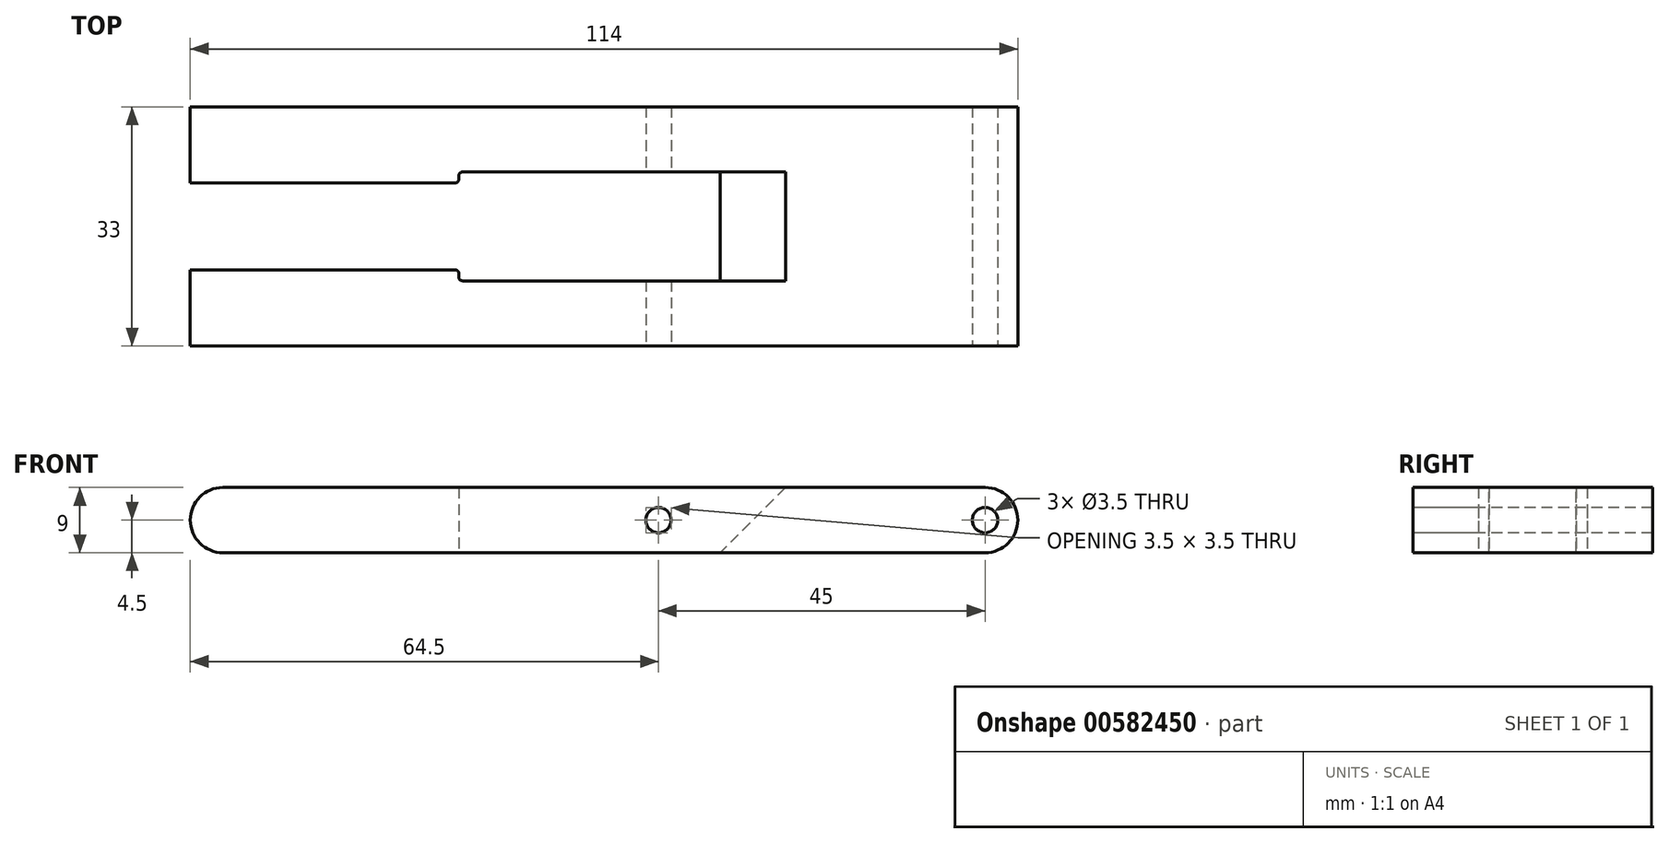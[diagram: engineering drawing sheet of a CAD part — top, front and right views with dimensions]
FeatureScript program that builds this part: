
annotation { "Feature Type Name" : "Feature", "Feature Type Description" : "" }
export const myFeature = defineFeature(function(context is Context, id is Id, definition is map)
    precondition{}
    {
        {
            var Q0;
            Q0=qCreatedBy(makeId("Front.planeOp"),FACE);
            var sketch = newSketch(context, id + "F0", { "sketchPlane" : qUnion([Q0])});
            skLineSegment(sketch, "E0", {"start": v(-52.5, 0) * mm, "end": v(52.5, 0) * mm});
            skLineSegment(sketch, "E1", {"start": v(-52.5, 9) * mm, "end": v(52.5, 9) * mm});
            skArc(sketch, "E2", {"start": v(52.5, 0) * mm, "mid": v(57, 4.5) * mm, "end": v(52.5, 9) * mm});
            skArc(sketch, "E3", {"start": v(-52.5, 9) * mm, "mid": v(-57, 4.5) * mm, "end": v(-52.5, 0) * mm});
            skSolve(sketch);
        }
        {
            var Q0;
            Q0 = qSketchRegion(id + "F0", true);
            extrude(context, id + "F1", {"entities" : qUnion([Q0]), "endBound" : BoundingType.SYMMETRIC, "depth" : 33 * mm, "offsetDistance" : 25 * mm});
        }
        {
            var Q0;
            Q0=makeQuery(id+"F1.opExtrude","CAP_FACE",FACE,{"disambiguationData":[OSD([sQuery(id+"F0.wireOp",EDGE,"aJSWKm7K-i3MK-chJk-4c2A-e9u8y67YIx2B"),sQuery(id+"F0.wireOp",EDGE,"E0"),sQuery(id+"F0.wireOp",EDGE,"E1"),sQuery(id+"F0.wireOp",EDGE,"E2")])],"isStart":false});
            var sketch = newSketch(context, id + "F2", { "sketchPlane" : qUnion([Q0])});
            skLineSegment(sketch, "E4.bottom", {"start": v(52.5, 4.5) * mm, "end": v(7.5, 4.5) * mm});
            skLineSegment(sketch, "E4.top", {"start": v(52.5, 14.5) * mm, "end": v(7.5, 14.5) * mm});
            skLineSegment(sketch, "E4.left", {"start": v(52.5, 4.5) * mm, "end": v(52.5, 14.5) * mm});
            skLineSegment(sketch, "E4.right", {"start": v(7.5, 4.5) * mm, "end": v(7.5, 14.5) * mm});
            skSolve(sketch);
        }
        {
            var Q0;
            Q0=sQuery(id+"F2.wireOp",VERTEX,"E4.right.start");
            var Q1;
            Q1=sQuery(id+"F2.wireOp",VERTEX,"E4.left.start");
            var Q2;
            Q2=makeQuery(id+"F1.opExtrude","SWEPT_BODY",BODY,{"disambiguationData":[OSD([sQuery(id+"F0.wireOp",EDGE,"aJSWKm7K-i3MK-chJk-4c2A-e9u8y67YIx2B"),sQuery(id+"F0.wireOp",EDGE,"E0"),sQuery(id+"F0.wireOp",EDGE,"E1"),sQuery(id+"F0.wireOp",EDGE,"E2")])]});
            hole(context, id + "F3", {"style" : HoleStyle.SIMPLE, "endStyle" : HoleEndStyle.THROUGH, "holeDiameter" : 3.5 * mm, "majorDiameter" : 5 * mm, "tappedDepth" : 12 * mm, "tapClearance" : 3, "locations" : qUnion([Q0, Q1]), "scope" : qUnion([Q2])});
        }
        {
            var Q0;
            Q0=qCreatedBy(makeId("Top.planeOp"),FACE);
            var sketch = newSketch(context, id + "F4", { "sketchPlane" : qUnion([Q0])});
            skLineSegment(sketch, "E5.bottom", {"start": v(-20, 7.5) * mm, "end": v(15, 7.5) * mm});
            skLineSegment(sketch, "E5.top", {"start": v(-20, -7.5) * mm, "end": v(15, -7.5) * mm});
            skLineSegment(sketch, "E5.left", {"start": v(-20, 7.5) * mm, "end": v(-20, -7.5) * mm});
            skLineSegment(sketch, "E5.right", {"start": v(15, 7.5) * mm, "end": v(15, -7.5) * mm});
            skLineSegment(sketch, "E6.bottom", {"start": v(-60, 6) * mm, "end": v(-20, 6) * mm});
            skLineSegment(sketch, "E6.top", {"start": v(-60, -6) * mm, "end": v(-20, -6) * mm});
            skLineSegment(sketch, "E6.left", {"start": v(-60, 6) * mm, "end": v(-60, -6) * mm});
            skLineSegment(sketch, "E6.right", {"start": v(-20, 6) * mm, "end": v(-20, -6) * mm});
            skSolve(sketch);
        }
        {
            var Q0;
            Q0 = qSketchRegion(id + "F4", true);
            extrude(context, id + "F5", {"entities" : qUnion([Q0]), "depth" : 25 * mm, "offsetDistance" : 25 * mm});
        }
        {
            var Q0;
            Q0=makeQuery(id+"F5.opExtrude","SWEPT_BODY",BODY,{"disambiguationData":[OSD([sQuery(id+"F63sIpcFp3KkyEQ_1.wireOp",EDGE,"vlWsCU3u-YBZQ-iikB-UPRL-M2tObz70Hnuf.bottom"),sQuery(id+"F63sIpcFp3KkyEQ_1.wireOp",EDGE,"vlWsCU3u-YBZQ-iikB-UPRL-M2tObz70Hnuf.top"),sQuery(id+"F63sIpcFp3KkyEQ_1.wireOp",EDGE,"vlWsCU3u-YBZQ-iikB-UPRL-M2tObz70Hnuf.left"),sQuery(id+"F63sIpcFp3KkyEQ_1.wireOp",EDGE,"vlWsCU3u-YBZQ-iikB-UPRL-M2tObz70Hnuf.right")])]});
            var Q1;
            Q1=makeQuery(id+"F5.opExtrude","SWEPT_BODY",BODY,{"disambiguationData":[OSD([sQuery(id+"F4.wireOp",EDGE,"E5.bottom"),sQuery(id+"F4.wireOp",EDGE,"E5.top"),sQuery(id+"F4.wireOp",EDGE,"E5.left"),sQuery(id+"F4.wireOp",EDGE,"E5.right")])]});
            var Q2;
            Q2=makeQuery(id+"F1.opExtrude","SWEPT_BODY",BODY,{"disambiguationData":[OSD([sQuery(id+"F0.wireOp",EDGE,"aJSWKm7K-i3MK-chJk-4c2A-e9u8y67YIx2B"),sQuery(id+"F0.wireOp",EDGE,"E0"),sQuery(id+"F0.wireOp",EDGE,"E1"),sQuery(id+"F0.wireOp",EDGE,"E2")])]});
            booleanBodies(context, id + "F6", {"operationType" : BooleanOperationType.SUBTRACTION, "tools" : qUnion([Q0, Q1]), "targets" : qUnion([Q2])});
        }
        {
            var Q0;
            Q0=makeQuery(id+"F6.opBoolean","INTERSECT",EDGE,{"derivedFrom":[makeQuery(id+"F1.opExtrude","SWEPT_FACE",FACE,{"disambiguationData":[OSD([sQuery(id+"F0.wireOp",EDGE,"E1")])]}),makeQuery(id+"F5.opExtrude","SWEPT_FACE",FACE,{"disambiguationData":[OSD([sQuery(id+"F4.wireOp",EDGE,"E5.right")])]})]});
            chamfer(context, id + "F7", {"entities" : qUnion([Q0]), "width" : 10 * mm, "tangentPropagation" : true});
        }
        {
            var Q0;
            Q0=makeQuery(id+"F6.opBoolean","COPY",EDGE,{"derivedFrom":makeQuery(id+"F5.opExtrude","SWEPT_EDGE",EDGE,{"disambiguationData":[OSD([sQuery(id+"F4.wireOp",EDGE,"E5.bottom"),sQuery(id+"F4.wireOp",EDGE,"E5.left")])]})});
            var Q1;
            Q1=makeQuery(id+"F6.opBoolean","COPY",EDGE,{"derivedFrom":makeQuery(id+"F5.opExtrude","SWEPT_EDGE",EDGE,{"disambiguationData":[OSD([sQuery(id+"F4.wireOp",EDGE,"E5.left"),sQuery(id+"F4.wireOp",EDGE,"E6.bottom"),sQuery(id+"F4.wireOp",EDGE,"E6.right")])]})});
            var Q2;
            Q2=makeQuery(id+"F6.opBoolean","COPY",EDGE,{"derivedFrom":makeQuery(id+"F5.opExtrude","SWEPT_EDGE",EDGE,{"disambiguationData":[OSD([sQuery(id+"F4.wireOp",EDGE,"E5.top"),sQuery(id+"F4.wireOp",EDGE,"E5.left")])]})});
            var Q3;
            Q3=makeQuery(id+"F6.opBoolean","COPY",EDGE,{"derivedFrom":makeQuery(id+"F5.opExtrude","SWEPT_EDGE",EDGE,{"disambiguationData":[OSD([sQuery(id+"F4.wireOp",EDGE,"E5.left"),sQuery(id+"F4.wireOp",EDGE,"E6.top"),sQuery(id+"F4.wireOp",EDGE,"E6.right")])]})});
            fillet(context, id + "F8", {"entities" : qUnion([Q0, Q1, Q2, Q3]), "radius" : 0.5 * mm, "tangentPropagation" : true, "allowEdgeOverflow" : false});
        }
    });
